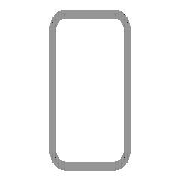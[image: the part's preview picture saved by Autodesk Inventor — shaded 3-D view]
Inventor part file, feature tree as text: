
AUTODESK INVENTOR PART (.ipt)
format: ipt  version: 2025 (Build 290162010, 162A)  size: 142,336 bytes
history: native  units: mm (DEFAULTED — no unit token found)
features: other x4, plane x2, split x1, sketch x1
ambient origin geometry x8: Origin, YZ Plane, XZ Plane, XY Plane, X Axis, Y Axis, Z Axis, Center Point
bodies: Solid1 (feature_tree), Body (feature_tree)
feature tree (8):
  parser-record x1  (decoder bookkeeping rows leaked as tree rows — omitted from the tree; the rows remain in map.json)
  other  "Driven Length"
  other  "Start Plane"
  other  "End Plane"
  plane  "Work Plane4"
  split  "Split1"
  sketch  "Sketch3"  dims[d3=793.237711mm d4=0.0mm d7=4.0mm d9=20.0mm d11=40.0mm d12=2.0mm d13=-0.0mm d14=793.237711mm d15=10.0mm d16=20.0mm d17=90.0deg d18=793.237711mm]
  plane  "Work Plane3"
